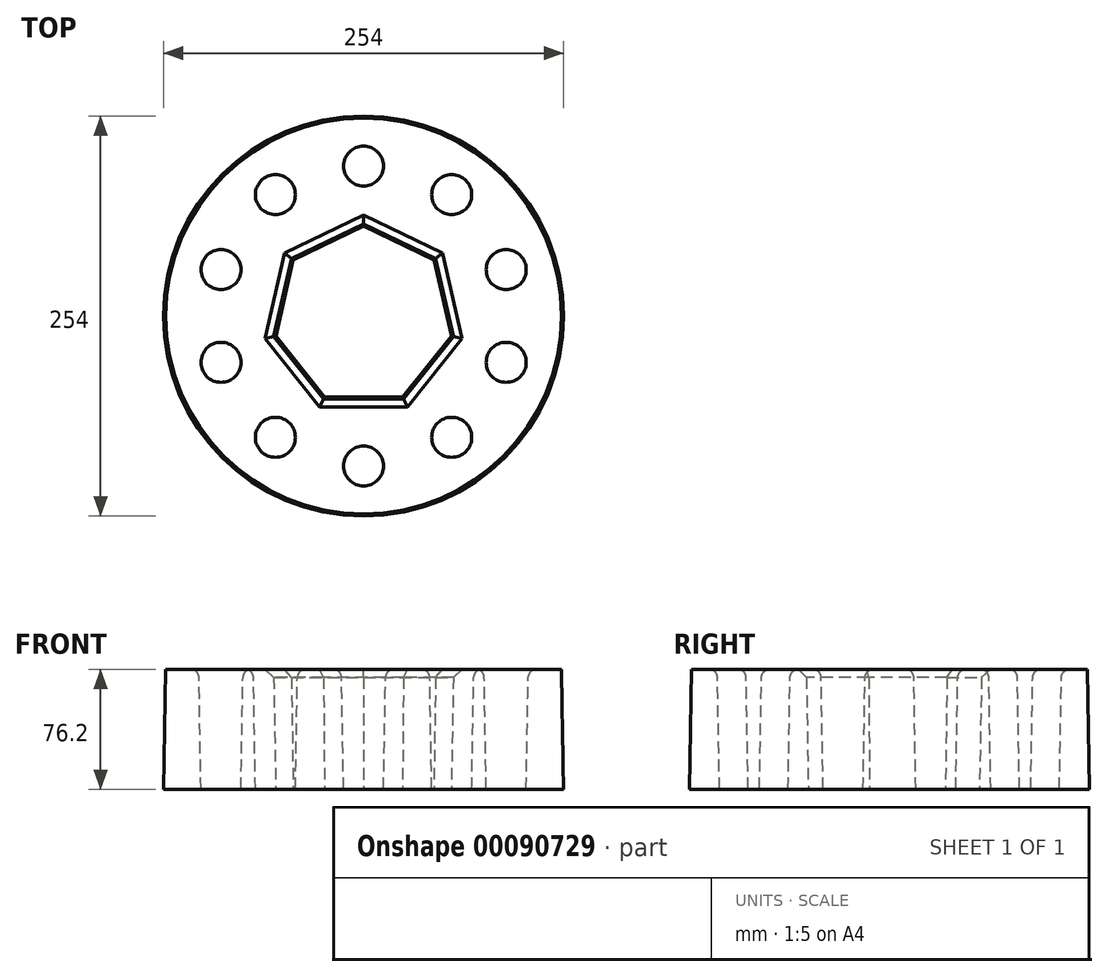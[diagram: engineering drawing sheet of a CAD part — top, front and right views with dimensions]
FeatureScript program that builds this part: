
annotation { "Feature Type Name" : "Feature", "Feature Type Description" : "" }
export const myFeature = defineFeature(function(context is Context, id is Id, definition is map)
    precondition{}
    {
        {
            var Q0;
            Q0=qCreatedBy(makeId("Top.planeOp"),FACE);
            var sketch = newSketch(context, id + "F0", { "sketchPlane" : qUnion([Q0])});
            skCircle(sketch, "E0", {"center": v(0, 0) * mm, "radius": 127 * mm});
            skCircle(sketch, "E1.cCircle", {"center": v(0, 0) * mm, "radius": 57.15 * mm, "construction": true});
            skLineSegment(sketch, "E1.0", {"start": v(0, 57.15) * mm, "end": v(44.68, 35.63) * mm});
            skLineSegment(sketch, "E1.1", {"start": v(44.68, 35.63) * mm, "end": v(55.72, -12.72) * mm});
            skLineSegment(sketch, "E1.2", {"start": v(55.72, -12.72) * mm, "end": v(24.8, -51.5) * mm});
            skLineSegment(sketch, "E1.3", {"start": v(24.8, -51.5) * mm, "end": v(-24.8, -51.5) * mm});
            skLineSegment(sketch, "E1.4", {"start": v(-24.8, -51.5) * mm, "end": v(-55.72, -12.72) * mm});
            skLineSegment(sketch, "E1.5", {"start": v(-55.72, -12.72) * mm, "end": v(-44.68, 35.63) * mm});
            skLineSegment(sketch, "E1.6", {"start": v(-44.68, 35.63) * mm, "end": v(0, 57.15) * mm});
            skCircle(sketch, "E2", {"center": v(0, 95.25) * mm, "radius": 12.7 * mm});
            skCircle(sketch, "E3.1.0", {"center": v(-55.99, 77.06) * mm, "radius": 12.7 * mm});
            skCircle(sketch, "E3.2.0", {"center": v(-90.59, 29.43) * mm, "radius": 12.7 * mm});
            skCircle(sketch, "E3.3.0", {"center": v(-90.59, -29.43) * mm, "radius": 12.7 * mm});
            skCircle(sketch, "E3.4.0", {"center": v(-55.99, -77.06) * mm, "radius": 12.7 * mm});
            skCircle(sketch, "E3.5.0", {"center": v(0, -95.25) * mm, "radius": 12.7 * mm});
            skCircle(sketch, "E3.6.0", {"center": v(55.99, -77.06) * mm, "radius": 12.7 * mm});
            skCircle(sketch, "E3.7.0", {"center": v(90.59, -29.43) * mm, "radius": 12.7 * mm});
            skCircle(sketch, "E3.8.0", {"center": v(90.59, 29.43) * mm, "radius": 12.7 * mm});
            skCircle(sketch, "E3.9.0", {"center": v(55.99, 77.06) * mm, "radius": 12.7 * mm});
            skSolve(sketch);
        }
        {
            var Q0;
            Q0=makeQuery(id+"F0.imprint","IMPRINT",FACE,{"disambiguationData":[TD([[makeQuery(id+"F0.imprint","IMPRINT",EDGE,{"derivedFrom":sQuery(id+"F0.wireOp",EDGE,"E0")}),1.0]])]});
            extrude(context, id + "F1", {"entities" : qUnion([Q0]), "depth" : 76.2 * mm, "hasDraft" : true, "draftAngle" : 1 * degree, "draftPullDirection" : true});
        }
        {
            var Q0;
            Q0=makeQuery(id+"F1.opExtrude","CAP_EDGE",EDGE,{"disambiguationData":[OSD([sQuery(id+"F0.wireOp",EDGE,"E1.0")])],"isStart":false});
            var Q1;
            Q1=makeQuery(id+"F1.opExtrude","CAP_EDGE",EDGE,{"disambiguationData":[OSD([sQuery(id+"F0.wireOp",EDGE,"E1.1")])],"isStart":false});
            var Q2;
            Q2=makeQuery(id+"F1.opExtrude","CAP_EDGE",EDGE,{"disambiguationData":[OSD([sQuery(id+"F0.wireOp",EDGE,"E1.2")])],"isStart":false});
            var Q3;
            Q3=makeQuery(id+"F1.opExtrude","CAP_EDGE",EDGE,{"disambiguationData":[OSD([sQuery(id+"F0.wireOp",EDGE,"E1.3")])],"isStart":false});
            var Q4;
            Q4=makeQuery(id+"F1.opExtrude","CAP_EDGE",EDGE,{"disambiguationData":[OSD([sQuery(id+"F0.wireOp",EDGE,"E1.4")])],"isStart":false});
            var Q5;
            Q5=makeQuery(id+"F1.opExtrude","CAP_EDGE",EDGE,{"disambiguationData":[OSD([sQuery(id+"F0.wireOp",EDGE,"E1.5")])],"isStart":false});
            var Q6;
            Q6=makeQuery(id+"F1.opExtrude","CAP_EDGE",EDGE,{"disambiguationData":[OSD([sQuery(id+"F0.wireOp",EDGE,"E1.6")])],"isStart":false});
            chamfer(context, id + "F2", {"entities" : qUnion([Q0, Q1, Q2, Q3, Q4, Q5, Q6]), "width" : 5.08 * mm, "tangentPropagation" : true});
        }
        {
            var Q0;
            Q0=makeQuery(id+"F1.opExtrude","CAP_EDGE",EDGE,{"disambiguationData":[OSD([sQuery(id+"F0.wireOp",EDGE,"E3.8.0")])],"isStart":false});
            var Q1;
            Q1=makeQuery(id+"F1.opExtrude","CAP_EDGE",EDGE,{"disambiguationData":[OSD([sQuery(id+"F0.wireOp",EDGE,"E3.7.0")])],"isStart":false});
            var Q2;
            Q2=makeQuery(id+"F1.opExtrude","CAP_EDGE",EDGE,{"disambiguationData":[OSD([sQuery(id+"F0.wireOp",EDGE,"E3.6.0")])],"isStart":false});
            var Q3;
            Q3=makeQuery(id+"F1.opExtrude","CAP_EDGE",EDGE,{"disambiguationData":[OSD([sQuery(id+"F0.wireOp",EDGE,"E3.5.0")])],"isStart":false});
            var Q4;
            Q4=makeQuery(id+"F1.opExtrude","CAP_EDGE",EDGE,{"disambiguationData":[OSD([sQuery(id+"F0.wireOp",EDGE,"E3.4.0")])],"isStart":false});
            var Q5;
            Q5=makeQuery(id+"F1.opExtrude","CAP_EDGE",EDGE,{"disambiguationData":[OSD([sQuery(id+"F0.wireOp",EDGE,"E3.3.0")])],"isStart":false});
            var Q6;
            Q6=makeQuery(id+"F1.opExtrude","CAP_EDGE",EDGE,{"disambiguationData":[OSD([sQuery(id+"F0.wireOp",EDGE,"E3.2.0")])],"isStart":false});
            var Q7;
            Q7=makeQuery(id+"F1.opExtrude","CAP_EDGE",EDGE,{"disambiguationData":[OSD([sQuery(id+"F0.wireOp",EDGE,"E3.1.0")])],"isStart":false});
            var Q8;
            Q8=makeQuery(id+"F1.opExtrude","CAP_EDGE",EDGE,{"disambiguationData":[OSD([sQuery(id+"F0.wireOp",EDGE,"E2")])],"isStart":false});
            var Q9;
            Q9=makeQuery(id+"F1.opExtrude","CAP_EDGE",EDGE,{"disambiguationData":[OSD([sQuery(id+"F0.wireOp",EDGE,"E3.9.0")])],"isStart":false});
            fillet(context, id + "F3", {"entities" : qUnion([Q0, Q1, Q2, Q3, Q4, Q5, Q6, Q7, Q8, Q9]), "radius" : 5.08 * mm, "tangentPropagation" : true, "allowEdgeOverflow" : false});
        }
    });
